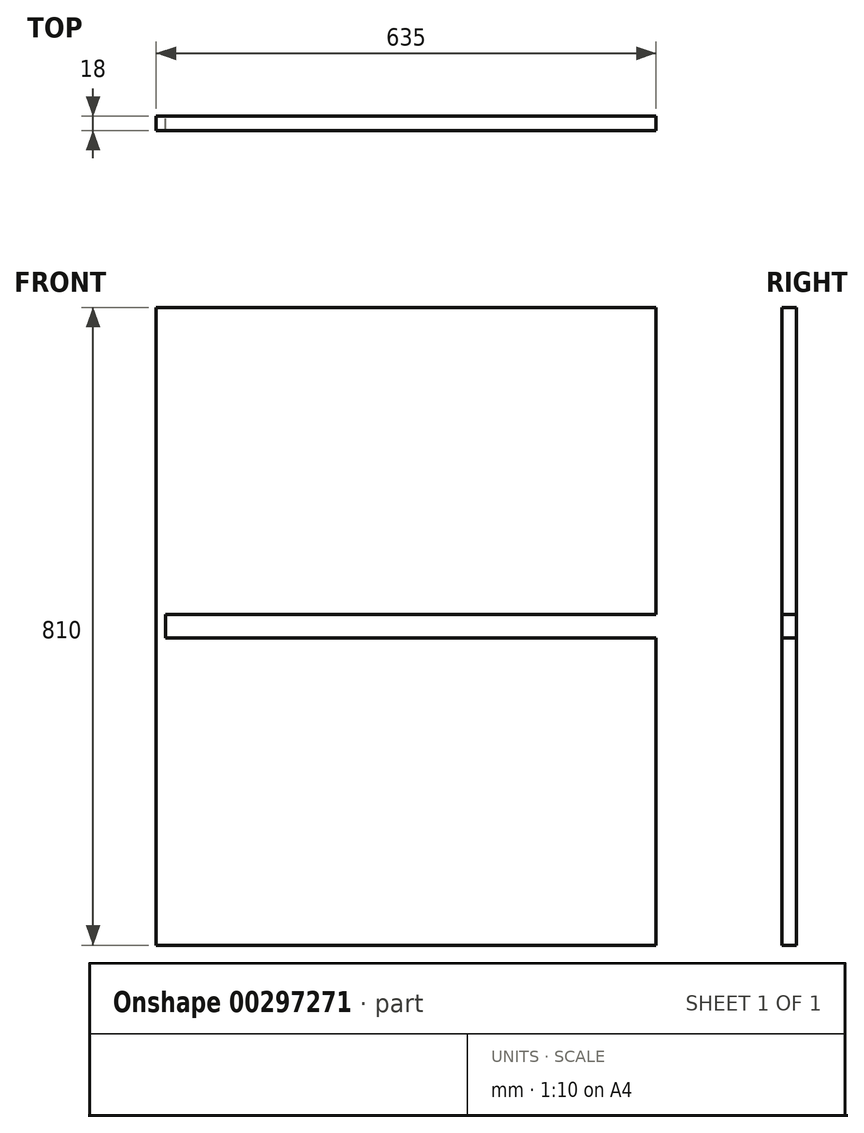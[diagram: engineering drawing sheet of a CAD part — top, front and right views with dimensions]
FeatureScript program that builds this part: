
annotation { "Feature Type Name" : "Feature", "Feature Type Description" : "" }
export const myFeature = defineFeature(function(context is Context, id is Id, definition is map)
    precondition{}
    {
        {
            var Q0;
            Q0=qCreatedBy(makeId("Front.planeOp"),FACE);
            var sketch = newSketch(context, id + "F0", { "sketchPlane" : qUnion([Q0])});
            skLineSegment(sketch, "E0.bottom", {"start": v(-317.5, 405) * mm, "end": v(317.5, 405) * mm});
            skLineSegment(sketch, "E0.top", {"start": v(-317.5, -405) * mm, "end": v(317.5, -405) * mm});
            skLineSegment(sketch, "E0.left", {"start": v(-317.5, 405) * mm, "end": v(-317.5, -405) * mm});
            skLineSegment(sketch, "E0.right", {"start": v(317.5, 405) * mm, "end": v(317.5, -405) * mm});
            skPoint(sketch, "E0.middle", {"position": v(0, 0) * mm});
            skSolve(sketch);
        }
        {
            var Q0;
            Q0=qSketchRegion(id+"F0",true);
            extrude(context, id + "F1", {"entities" : qUnion([Q0]), "depth" : 18 * mm});
        }
        {
            var Q0;
            Q0=makeQuery(id+"F1.opExtrude","SWEPT_FACE",FACE,{"disambiguationData":[OSD([sQuery(id+"F0.wireOp",EDGE,"E0.right")])]});
            var sketch = newSketch(context, id + "F2", { "sketchPlane" : qUnion([Q0])});
            skLineSegment(sketch, "E1.bottom", {"start": v(-18, -15) * mm, "end": v(0, -15) * mm});
            skLineSegment(sketch, "E1.top", {"start": v(-18, 15) * mm, "end": v(0, 15) * mm});
            skLineSegment(sketch, "E1.left", {"start": v(-18, -15) * mm, "end": v(-18, 15) * mm});
            skLineSegment(sketch, "E1.right", {"start": v(0, -15) * mm, "end": v(0, 15) * mm});
            skSolve(sketch);
        }
        {
            var Q0;
            Q0=qSketchRegion(id+"F2",true);
            extrude(context, id + "F3", {"entities" : qUnion([Q0]), "operationType" : NewBodyOperationType.REMOVE, "oppositeDirection" : true, "depth" : 623 * mm});
        }
    });
